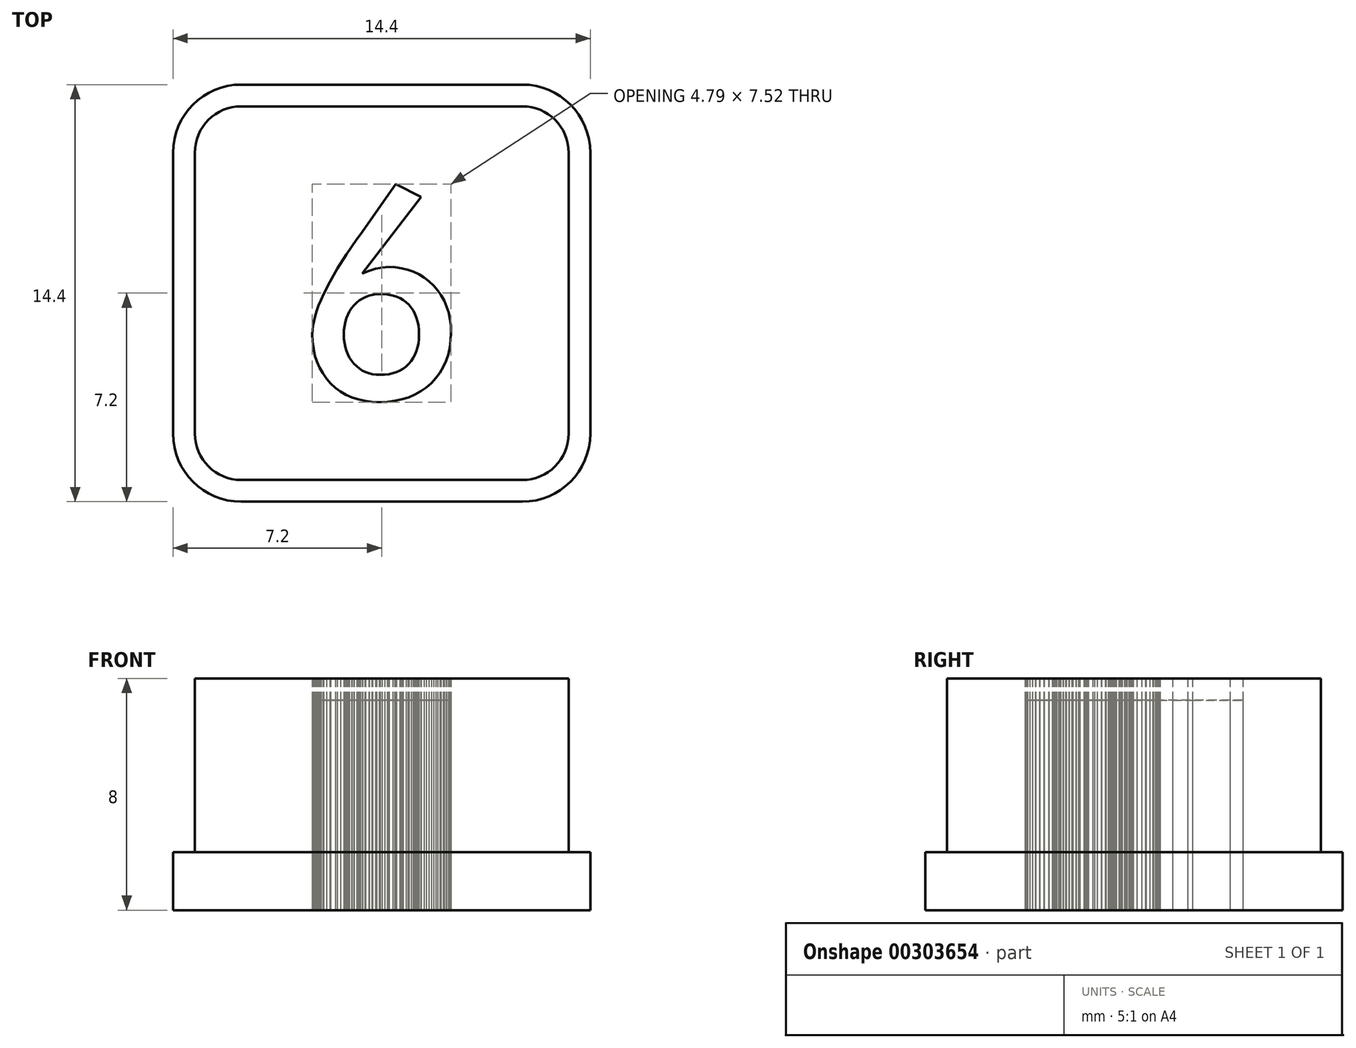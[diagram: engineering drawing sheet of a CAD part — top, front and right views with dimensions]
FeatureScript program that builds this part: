
annotation { "Feature Type Name" : "Feature", "Feature Type Description" : "" }
export const myFeature = defineFeature(function(context is Context, id is Id, definition is map)
    precondition{}
    {
        {
            var Q0;
            Q0=qCreatedBy(makeId("Top.planeOp"),FACE);
            var sketch = newSketch(context, id + "F0", { "sketchPlane" : qUnion([Q0])});
            skArc(sketch, "E0", {"start": v(4.85, -6.45) * mm, "mid": v(5.98, -5.98) * mm, "end": v(6.45, -4.85) * mm});
            skLineSegment(sketch, "E1", {"start": v(6.45, -4.85) * mm, "end": v(6.45, 4.85) * mm});
            skArc(sketch, "E2", {"start": v(6.45, 4.85) * mm, "mid": v(5.98, 5.98) * mm, "end": v(4.85, 6.45) * mm});
            skLineSegment(sketch, "E3", {"start": v(4.85, 6.45) * mm, "end": v(-4.85, 6.45) * mm});
            skArc(sketch, "E4", {"start": v(-4.85, 6.45) * mm, "mid": v(-5.98, 5.98) * mm, "end": v(-6.45, 4.85) * mm});
            skLineSegment(sketch, "E5", {"start": v(-6.45, 4.85) * mm, "end": v(-6.45, -4.85) * mm});
            skArc(sketch, "E6", {"start": v(-6.45, -4.85) * mm, "mid": v(-5.98, -5.98) * mm, "end": v(-4.85, -6.45) * mm});
            skLineSegment(sketch, "E7", {"start": v(-4.85, -6.45) * mm, "end": v(4.85, -6.45) * mm});
            skArc(sketch, "E8", {"start": v(-4.85, 7.2) * mm, "mid": v(-6.51, 6.51) * mm, "end": v(-7.2, 4.85) * mm});
            skLineSegment(sketch, "E9", {"start": v(-7.2, 4.85) * mm, "end": v(-7.2, -4.85) * mm});
            skArc(sketch, "E10", {"start": v(-7.2, -4.85) * mm, "mid": v(-6.51, -6.51) * mm, "end": v(-4.85, -7.2) * mm});
            skLineSegment(sketch, "E11", {"start": v(-4.85, -7.2) * mm, "end": v(4.85, -7.2) * mm});
            skArc(sketch, "E12", {"start": v(4.85, -7.2) * mm, "mid": v(6.51, -6.51) * mm, "end": v(7.2, -4.85) * mm});
            skLineSegment(sketch, "E13", {"start": v(7.2, -4.85) * mm, "end": v(7.2, 4.85) * mm});
            skArc(sketch, "E14", {"start": v(7.2, 4.85) * mm, "mid": v(6.51, 6.51) * mm, "end": v(4.85, 7.2) * mm});
            skLineSegment(sketch, "E15", {"start": v(4.85, 7.2) * mm, "end": v(-4.85, 7.2) * mm});
            skLineSegment(sketch, "E16", {"start": v(-1.3, -1.43) * mm, "end": v(-1.3, -1.58) * mm});
            skLineSegment(sketch, "E17", {"start": v(-1.3, -1.58) * mm, "end": v(-1.29, -1.73) * mm});
            skLineSegment(sketch, "E18", {"start": v(-1.29, -1.73) * mm, "end": v(-1.26, -1.86) * mm});
            skLineSegment(sketch, "E19", {"start": v(-1.26, -1.86) * mm, "end": v(-1.22, -2) * mm});
            skLineSegment(sketch, "E20", {"start": v(-1.22, -2) * mm, "end": v(-1.17, -2.11) * mm});
            skLineSegment(sketch, "E21", {"start": v(-1.17, -2.11) * mm, "end": v(-1.11, -2.23) * mm});
            skLineSegment(sketch, "E22", {"start": v(-1.11, -2.23) * mm, "end": v(-1.04, -2.34) * mm});
            skLineSegment(sketch, "E23", {"start": v(-1.04, -2.34) * mm, "end": v(-0.96, -2.44) * mm});
            skLineSegment(sketch, "E24", {"start": v(-0.96, -2.44) * mm, "end": v(-0.87, -2.53) * mm});
            skLineSegment(sketch, "E25", {"start": v(-0.87, -2.53) * mm, "end": v(-0.77, -2.6) * mm});
            skLineSegment(sketch, "E26", {"start": v(-0.77, -2.6) * mm, "end": v(-0.67, -2.67) * mm});
            skLineSegment(sketch, "E27", {"start": v(-0.67, -2.67) * mm, "end": v(-0.56, -2.72) * mm});
            skLineSegment(sketch, "E28", {"start": v(-0.56, -2.72) * mm, "end": v(-0.44, -2.76) * mm});
            skLineSegment(sketch, "E29", {"start": v(-0.44, -2.76) * mm, "end": v(-0.32, -2.8) * mm});
            skLineSegment(sketch, "E30", {"start": v(-0.32, -2.8) * mm, "end": v(-0.2, -2.81) * mm});
            skLineSegment(sketch, "E31", {"start": v(-0.2, -2.81) * mm, "end": v(-0.05, -2.82) * mm});
            skLineSegment(sketch, "E32", {"start": v(-0.05, -2.82) * mm, "end": v(0.1, -2.81) * mm});
            skLineSegment(sketch, "E33", {"start": v(0.1, -2.81) * mm, "end": v(0.24, -2.8) * mm});
            skLineSegment(sketch, "E34", {"start": v(0.24, -2.8) * mm, "end": v(0.38, -2.77) * mm});
            skLineSegment(sketch, "E35", {"start": v(0.38, -2.77) * mm, "end": v(0.5, -2.73) * mm});
            skLineSegment(sketch, "E36", {"start": v(0.5, -2.73) * mm, "end": v(0.62, -2.67) * mm});
            skLineSegment(sketch, "E37", {"start": v(0.62, -2.67) * mm, "end": v(0.73, -2.6) * mm});
            skLineSegment(sketch, "E38", {"start": v(0.73, -2.6) * mm, "end": v(0.84, -2.53) * mm});
            skLineSegment(sketch, "E39", {"start": v(0.84, -2.53) * mm, "end": v(0.93, -2.45) * mm});
            skLineSegment(sketch, "E40", {"start": v(0.93, -2.45) * mm, "end": v(1.01, -2.35) * mm});
            skLineSegment(sketch, "E41", {"start": v(1.01, -2.35) * mm, "end": v(1.09, -2.24) * mm});
            skLineSegment(sketch, "E42", {"start": v(1.09, -2.24) * mm, "end": v(1.15, -2.13) * mm});
            skLineSegment(sketch, "E43", {"start": v(1.15, -2.13) * mm, "end": v(1.2, -2) * mm});
            skLineSegment(sketch, "E44", {"start": v(1.2, -2) * mm, "end": v(1.24, -1.87) * mm});
            skLineSegment(sketch, "E45", {"start": v(1.24, -1.87) * mm, "end": v(1.27, -1.73) * mm});
            skLineSegment(sketch, "E46", {"start": v(1.27, -1.73) * mm, "end": v(1.28, -1.58) * mm});
            skLineSegment(sketch, "E47", {"start": v(1.28, -1.58) * mm, "end": v(1.29, -1.43) * mm});
            skLineSegment(sketch, "E48", {"start": v(1.29, -1.43) * mm, "end": v(1.28, -1.27) * mm});
            skLineSegment(sketch, "E49", {"start": v(1.28, -1.27) * mm, "end": v(1.27, -1.12) * mm});
            skLineSegment(sketch, "E50", {"start": v(1.27, -1.12) * mm, "end": v(1.24, -0.98) * mm});
            skLineSegment(sketch, "E51", {"start": v(1.24, -0.98) * mm, "end": v(1.2, -0.84) * mm});
            skLineSegment(sketch, "E52", {"start": v(1.2, -0.84) * mm, "end": v(1.15, -0.72) * mm});
            skLineSegment(sketch, "E53", {"start": v(1.15, -0.72) * mm, "end": v(1.09, -0.6) * mm});
            skLineSegment(sketch, "E54", {"start": v(1.09, -0.6) * mm, "end": v(1.02, -0.5) * mm});
            skLineSegment(sketch, "E55", {"start": v(1.02, -0.5) * mm, "end": v(0.93, -0.4) * mm});
            skLineSegment(sketch, "E56", {"start": v(0.93, -0.4) * mm, "end": v(0.84, -0.31) * mm});
            skLineSegment(sketch, "E57", {"start": v(0.84, -0.31) * mm, "end": v(0.74, -0.24) * mm});
            skLineSegment(sketch, "E58", {"start": v(0.74, -0.24) * mm, "end": v(0.63, -0.18) * mm});
            skLineSegment(sketch, "E59", {"start": v(0.63, -0.18) * mm, "end": v(0.51, -0.12) * mm});
            skLineSegment(sketch, "E60", {"start": v(0.51, -0.12) * mm, "end": v(0.39, -0.08) * mm});
            skLineSegment(sketch, "E61", {"start": v(0.39, -0.08) * mm, "end": v(0.25, -0.05) * mm});
            skLineSegment(sketch, "E62", {"start": v(0.25, -0.05) * mm, "end": v(0.1, -0.04) * mm});
            skLineSegment(sketch, "E63", {"start": v(0.1, -0.04) * mm, "end": v(-0.05, -0.03) * mm});
            skLineSegment(sketch, "E64", {"start": v(-0.05, -0.03) * mm, "end": v(-0.18, -0.04) * mm});
            skLineSegment(sketch, "E65", {"start": v(-0.18, -0.04) * mm, "end": v(-0.31, -0.06) * mm});
            skLineSegment(sketch, "E66", {"start": v(-0.31, -0.06) * mm, "end": v(-0.44, -0.09) * mm});
            skLineSegment(sketch, "E67", {"start": v(-0.44, -0.09) * mm, "end": v(-0.55, -0.13) * mm});
            skLineSegment(sketch, "E68", {"start": v(-0.55, -0.13) * mm, "end": v(-0.66, -0.18) * mm});
            skLineSegment(sketch, "E69", {"start": v(-0.66, -0.18) * mm, "end": v(-0.77, -0.25) * mm});
            skLineSegment(sketch, "E70", {"start": v(-0.77, -0.25) * mm, "end": v(-0.87, -0.33) * mm});
            skLineSegment(sketch, "E71", {"start": v(-0.87, -0.33) * mm, "end": v(-0.96, -0.42) * mm});
            skLineSegment(sketch, "E72", {"start": v(-0.96, -0.42) * mm, "end": v(-1.04, -0.52) * mm});
            skLineSegment(sketch, "E73", {"start": v(-1.04, -0.52) * mm, "end": v(-1.11, -0.63) * mm});
            skLineSegment(sketch, "E74", {"start": v(-1.11, -0.63) * mm, "end": v(-1.17, -0.74) * mm});
            skLineSegment(sketch, "E75", {"start": v(-1.17, -0.74) * mm, "end": v(-1.22, -0.86) * mm});
            skLineSegment(sketch, "E76", {"start": v(-1.22, -0.86) * mm, "end": v(-1.26, -1) * mm});
            skLineSegment(sketch, "E77", {"start": v(-1.26, -1) * mm, "end": v(-1.29, -1.13) * mm});
            skLineSegment(sketch, "E78", {"start": v(-1.29, -1.13) * mm, "end": v(-1.3, -1.28) * mm});
            skLineSegment(sketch, "E79", {"start": v(-1.3, -1.28) * mm, "end": v(-1.3, -1.43) * mm});
            skLineSegment(sketch, "E80", {"start": v(-0.67, 0.68) * mm, "end": v(-0.44, 0.77) * mm});
            skLineSegment(sketch, "E81", {"start": v(-0.44, 0.77) * mm, "end": v(-0.21, 0.84) * mm});
            skLineSegment(sketch, "E82", {"start": v(-0.21, 0.84) * mm, "end": v(0.02, 0.89) * mm});
            skLineSegment(sketch, "E83", {"start": v(0.02, 0.89) * mm, "end": v(0.24, 0.9) * mm});
            skLineSegment(sketch, "E84", {"start": v(0.24, 0.9) * mm, "end": v(0.47, 0.9) * mm});
            skLineSegment(sketch, "E85", {"start": v(0.47, 0.9) * mm, "end": v(0.69, 0.86) * mm});
            skLineSegment(sketch, "E86", {"start": v(0.69, 0.86) * mm, "end": v(0.9, 0.81) * mm});
            skLineSegment(sketch, "E87", {"start": v(0.9, 0.81) * mm, "end": v(1.1, 0.74) * mm});
            skLineSegment(sketch, "E88", {"start": v(1.1, 0.74) * mm, "end": v(1.28, 0.65) * mm});
            skLineSegment(sketch, "E89", {"start": v(1.28, 0.65) * mm, "end": v(1.46, 0.54) * mm});
            skLineSegment(sketch, "E90", {"start": v(1.46, 0.54) * mm, "end": v(1.63, 0.41) * mm});
            skLineSegment(sketch, "E91", {"start": v(1.63, 0.41) * mm, "end": v(1.79, 0.27) * mm});
            skLineSegment(sketch, "E92", {"start": v(1.79, 0.27) * mm, "end": v(1.93, 0.1) * mm});
            skLineSegment(sketch, "E93", {"start": v(1.93, 0.1) * mm, "end": v(2.05, -0.07) * mm});
            skLineSegment(sketch, "E94", {"start": v(2.05, -0.07) * mm, "end": v(2.16, -0.26) * mm});
            skLineSegment(sketch, "E95", {"start": v(2.16, -0.26) * mm, "end": v(2.24, -0.46) * mm});
            skLineSegment(sketch, "E96", {"start": v(2.24, -0.46) * mm, "end": v(2.3, -0.67) * mm});
            skLineSegment(sketch, "E97", {"start": v(2.3, -0.67) * mm, "end": v(2.36, -0.89) * mm});
            skLineSegment(sketch, "E98", {"start": v(2.36, -0.89) * mm, "end": v(2.38, -1.12) * mm});
            skLineSegment(sketch, "E99", {"start": v(2.38, -1.12) * mm, "end": v(2.4, -1.36) * mm});
            skLineSegment(sketch, "E100", {"start": v(2.4, -1.36) * mm, "end": v(2.38, -1.62) * mm});
            skLineSegment(sketch, "E101", {"start": v(2.38, -1.62) * mm, "end": v(2.35, -1.87) * mm});
            skLineSegment(sketch, "E102", {"start": v(2.35, -1.87) * mm, "end": v(2.3, -2.11) * mm});
            skLineSegment(sketch, "E103", {"start": v(2.3, -2.11) * mm, "end": v(2.22, -2.34) * mm});
            skLineSegment(sketch, "E104", {"start": v(2.22, -2.34) * mm, "end": v(2.13, -2.55) * mm});
            skLineSegment(sketch, "E105", {"start": v(2.13, -2.55) * mm, "end": v(2, -2.74) * mm});
            skLineSegment(sketch, "E106", {"start": v(2, -2.74) * mm, "end": v(1.87, -2.93) * mm});
            skLineSegment(sketch, "E107", {"start": v(1.87, -2.93) * mm, "end": v(1.71, -3.1) * mm});
            skLineSegment(sketch, "E108", {"start": v(1.71, -3.1) * mm, "end": v(1.53, -3.26) * mm});
            skLineSegment(sketch, "E109", {"start": v(1.53, -3.26) * mm, "end": v(1.34, -3.39) * mm});
            skLineSegment(sketch, "E110", {"start": v(1.34, -3.39) * mm, "end": v(1.14, -3.5) * mm});
            skLineSegment(sketch, "E111", {"start": v(1.14, -3.5) * mm, "end": v(0.92, -3.6) * mm});
            skLineSegment(sketch, "E112", {"start": v(0.92, -3.6) * mm, "end": v(0.7, -3.67) * mm});
            skLineSegment(sketch, "E113", {"start": v(0.7, -3.67) * mm, "end": v(0.45, -3.72) * mm});
            skLineSegment(sketch, "E114", {"start": v(0.45, -3.72) * mm, "end": v(0.19, -3.75) * mm});
            skLineSegment(sketch, "E115", {"start": v(0.19, -3.75) * mm, "end": v(-0.08, -3.76) * mm});
            skLineSegment(sketch, "E116", {"start": v(-0.08, -3.76) * mm, "end": v(-0.34, -3.75) * mm});
            skLineSegment(sketch, "E117", {"start": v(-0.34, -3.75) * mm, "end": v(-0.58, -3.72) * mm});
            skLineSegment(sketch, "E118", {"start": v(-0.58, -3.72) * mm, "end": v(-0.8, -3.67) * mm});
            skLineSegment(sketch, "E119", {"start": v(-0.8, -3.67) * mm, "end": v(-1.02, -3.6) * mm});
            skLineSegment(sketch, "E120", {"start": v(-1.02, -3.6) * mm, "end": v(-1.23, -3.5) * mm});
            skLineSegment(sketch, "E121", {"start": v(-1.23, -3.5) * mm, "end": v(-1.42, -3.4) * mm});
            skLineSegment(sketch, "E122", {"start": v(-1.42, -3.4) * mm, "end": v(-1.6, -3.27) * mm});
            skLineSegment(sketch, "E123", {"start": v(-1.6, -3.27) * mm, "end": v(-1.76, -3.12) * mm});
            skLineSegment(sketch, "E124", {"start": v(-1.76, -3.12) * mm, "end": v(-1.9, -2.95) * mm});
            skLineSegment(sketch, "E125", {"start": v(-1.9, -2.95) * mm, "end": v(-2.04, -2.77) * mm});
            skLineSegment(sketch, "E126", {"start": v(-2.04, -2.77) * mm, "end": v(-2.15, -2.57) * mm});
            skLineSegment(sketch, "E127", {"start": v(-2.15, -2.57) * mm, "end": v(-2.23, -2.37) * mm});
            skLineSegment(sketch, "E128", {"start": v(-2.23, -2.37) * mm, "end": v(-2.3, -2.15) * mm});
            skLineSegment(sketch, "E129", {"start": v(-2.3, -2.15) * mm, "end": v(-2.35, -1.92) * mm});
            skLineSegment(sketch, "E130", {"start": v(-2.35, -1.92) * mm, "end": v(-2.38, -1.67) * mm});
            skLineSegment(sketch, "E131", {"start": v(-2.38, -1.67) * mm, "end": v(-2.4, -1.42) * mm});
            skLineSegment(sketch, "E132", {"start": v(-2.4, -1.42) * mm, "end": v(-2.39, -1.27) * mm});
            skLineSegment(sketch, "E133", {"start": v(-2.39, -1.27) * mm, "end": v(-2.37, -1.12) * mm});
            skLineSegment(sketch, "E134", {"start": v(-2.37, -1.12) * mm, "end": v(-2.34, -0.96) * mm});
            skLineSegment(sketch, "E135", {"start": v(-2.34, -0.96) * mm, "end": v(-2.3, -0.8) * mm});
            skLineSegment(sketch, "E136", {"start": v(-2.3, -0.8) * mm, "end": v(-2.24, -0.62) * mm});
            skLineSegment(sketch, "E137", {"start": v(-2.24, -0.62) * mm, "end": v(-2.18, -0.43) * mm});
            skLineSegment(sketch, "E138", {"start": v(-2.18, -0.43) * mm, "end": v(-2.1, -0.24) * mm});
            skLineSegment(sketch, "E139", {"start": v(-2.1, -0.24) * mm, "end": v(-2.01, -0.04) * mm});
            skLineSegment(sketch, "E140", {"start": v(-2.01, -0.04) * mm, "end": v(-1.8, 0.39) * mm});
            skLineSegment(sketch, "E141", {"start": v(-1.8, 0.39) * mm, "end": v(-1.53, 0.85) * mm});
            skLineSegment(sketch, "E142", {"start": v(-1.53, 0.85) * mm, "end": v(-1.22, 1.34) * mm});
            skLineSegment(sketch, "E143", {"start": v(-1.22, 1.34) * mm, "end": v(-0.86, 1.86) * mm});
            skLineSegment(sketch, "E144", {"start": v(-0.86, 1.86) * mm, "end": v(-0.74, 2.02) * mm});
            skLineSegment(sketch, "E145", {"start": v(-0.74, 2.02) * mm, "end": v(0.49, 3.76) * mm});
            skLineSegment(sketch, "E146", {"start": v(0.49, 3.76) * mm, "end": v(1.36, 3.32) * mm});
            skLineSegment(sketch, "E147", {"start": v(1.36, 3.32) * mm, "end": v(-0.67, 0.68) * mm});
            skSolve(sketch);
        }
        {
            var Q0;
            Q0=makeQuery(id+"F0.imprint","IMPRINT",FACE,{"disambiguationData":[TD([[makeQuery(id+"F0.imprint","IMPRINT",EDGE,{"derivedFrom":sQuery(id+"F0.wireOp",EDGE,"E0")}),-1.0]])]});
            extrude(context, id + "F1", {"entities" : qUnion([Q0]), "depth" : 2 * mm});
        }
        {
            var Q0;
            Q0=makeQuery(id+"F0.imprint","IMPRINT",FACE,{"disambiguationData":[TD([[makeQuery(id+"F0.imprint","IMPRINT",EDGE,{"derivedFrom":sQuery(id+"F0.wireOp",EDGE,"E0")}),1.0]])]});
            var Q1;
            Q1=makeQuery(id+"F0.imprint","IMPRINT",FACE,{"disambiguationData":[TD([[makeQuery(id+"F0.imprint","IMPRINT",EDGE,{"derivedFrom":sQuery(id+"F0.wireOp",EDGE,"E16")}),1.0]])]});
            extrude(context, id + "F2", {"entities" : qUnion([Q0, Q1]), "operationType" : NewBodyOperationType.ADD, "depth" : 8 * mm});
        }
        {
            var Q0;
            Q0=makeQuery(id+"F0.imprint","IMPRINT",FACE,{"disambiguationData":[TD([[makeQuery(id+"F0.imprint","IMPRINT",EDGE,{"derivedFrom":sQuery(id+"F0.wireOp",EDGE,"E16")}),-1.0]])]});
            extrude(context, id + "F3", {"entities" : qUnion([Q0]), "depth" : 7.25 * mm});
        }
    });
